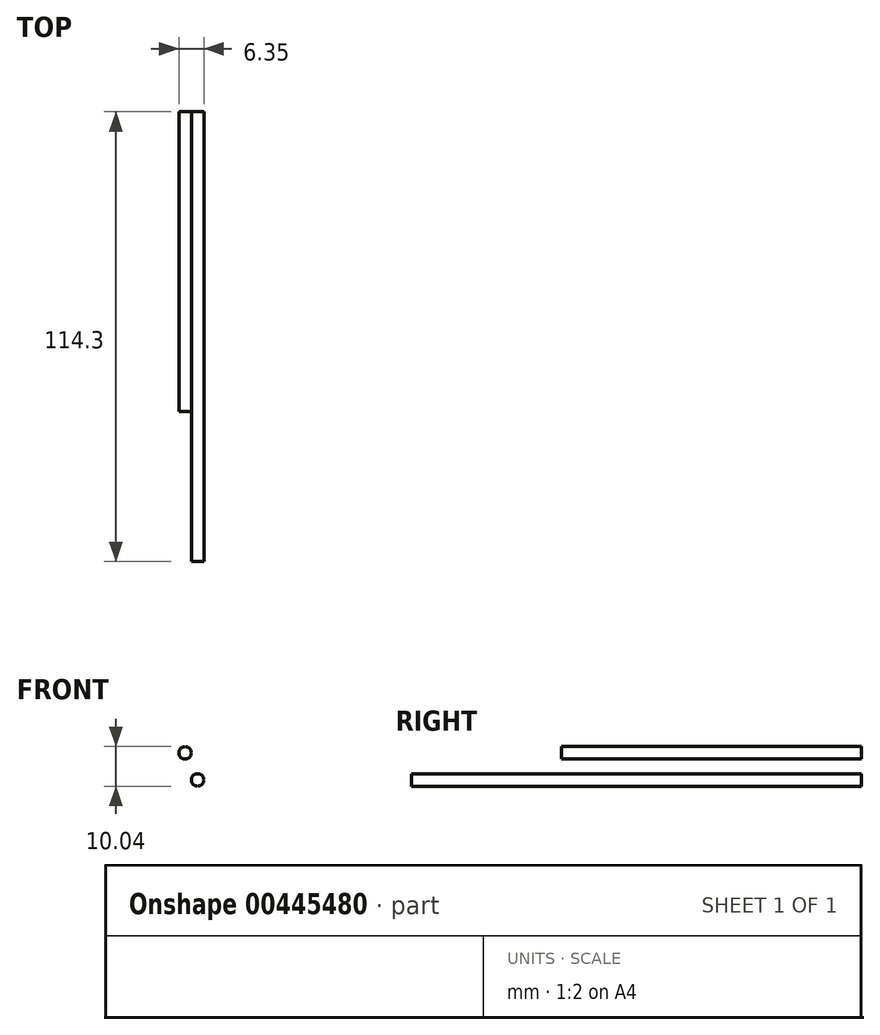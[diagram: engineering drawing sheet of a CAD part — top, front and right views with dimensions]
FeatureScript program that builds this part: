
annotation { "Feature Type Name" : "Feature", "Feature Type Description" : "" }
export const myFeature = defineFeature(function(context is Context, id is Id, definition is map)
    precondition{}
    {
        {
            var Q0;
            Q0=qCreatedBy(makeId("Front.planeOp"),FACE);
            var sketch = newSketch(context, id + "F0", { "sketchPlane" : qUnion([Q0])});
            skCircle(sketch, "E0", {"center": v(1.59, 55.9) * mm, "radius": 1.59 * mm});
            skSolve(sketch);
        }
        {
            var Q0;
            Q0 = qSketchRegion(id + "F0", true);
            extrude(context, id + "F1", {"entities" : qUnion([Q0]), "depth" : 76.2 * mm, "offsetDistance" : 25.4 * mm});
        }
        {
            var Q0;
            Q0=qCreatedBy(makeId("Front.planeOp"),FACE);
            var sketch = newSketch(context, id + "F2", { "sketchPlane" : qUnion([Q0])});
            skCircle(sketch, "E1", {"center": v(4.76, 49.03) * mm, "radius": 1.59 * mm});
            skSolve(sketch);
        }
        {
            var Q0;
            Q0 = qSketchRegion(id + "F2", true);
            extrude(context, id + "F3", {"entities" : qUnion([Q0]), "depth" : 114.3 * mm, "offsetDistance" : 25.4 * mm});
        }
    });
